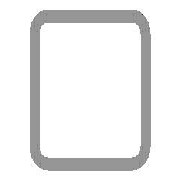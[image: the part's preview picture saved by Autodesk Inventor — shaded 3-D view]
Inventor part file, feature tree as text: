
AUTODESK INVENTOR PART (.ipt)
format: ipt  version: 2025 (Build 290162010, 162A)  size: 148,992 bytes
history: native  units: mm (DEFAULTED — no unit token found)
features: other x4, plane x3, split x2, sketch x1
ambient origin geometry x8: Origin, YZ Plane, XZ Plane, XY Plane, X Axis, Y Axis, Z Axis, Center Point
bodies: Solid1 (feature_tree), Body (feature_tree)
feature tree (10):
  parser-record x1  (decoder bookkeeping rows leaked as tree rows — omitted from the tree; the rows remain in map.json)
  other  "Driven Length"
  other  "Start Plane"
  other  "End Plane"
  plane  "Work Plane4"
  split  "Split1"
  plane  "Work Plane5"
  split  "Split2"
  sketch  "Sketch3"  dims[d3=849.577767mm d4=0.0mm d7=4.0mm d9=40.0mm d11=40.0mm d12=2.0mm d13=62.470912mm d14=912.048679mm d15=20.0mm d16=20.0mm d17=90.0deg d18=849.577767mm]
  plane  "Work Plane3"
